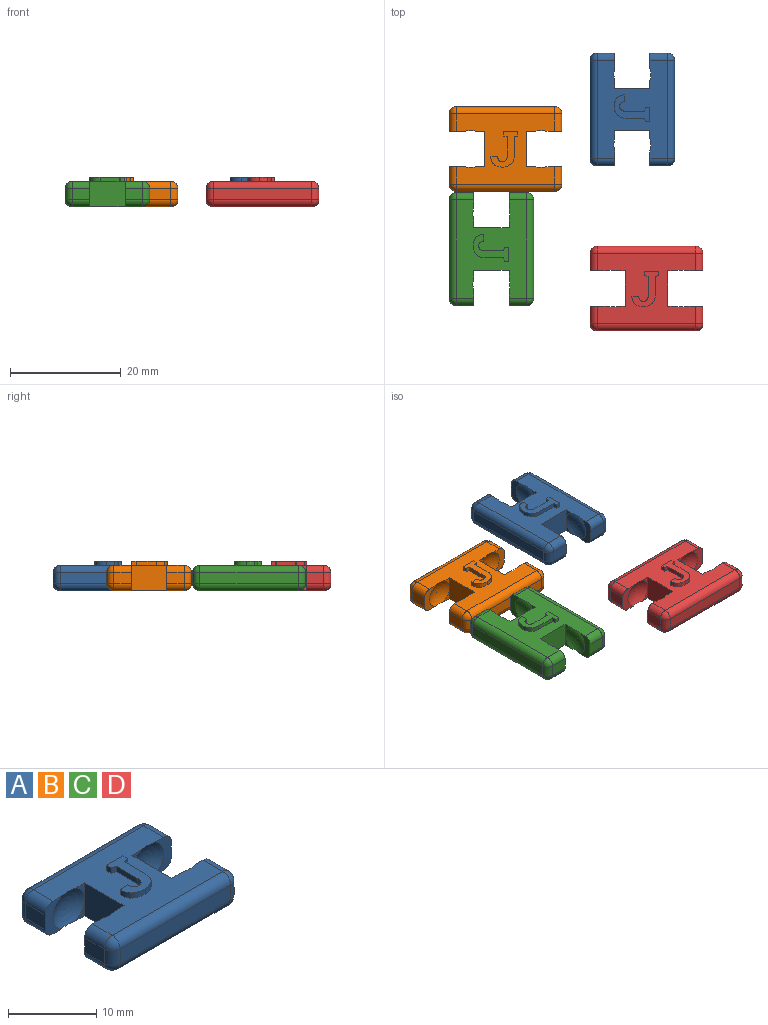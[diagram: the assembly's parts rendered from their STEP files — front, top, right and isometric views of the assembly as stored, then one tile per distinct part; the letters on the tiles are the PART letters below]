
ASSEMBLY  parts=4 mates=3
PART A: 68 faces, bbox 20.3x15.2x5.6 mm
  f0: plane 17.78x12.7mm, normal (0,0,1), area 148.5mm2, adj f2,f4,f6,f7,f9,f11,f14,f15
  f1: plane 17.78x12.7mm, normal (0,0,-1), area 160.4mm2, adj f2,f3,f4,f5,f7,f8,f9,f10
  f2: plane 4.57x2.7mm, normal (0,-1,0), area 7mm2, adj f0,f1,f13,f36,f37,f49
  f3: plane 2.29x1.43mm, normal (0,-1,0), area 0.9mm2, adj f1,f15,f49
  f4: plane 4.57x2.7mm, normal (0,1,0), area 7mm2, adj f0,f1,f16,f26,f27,f48
  f5: plane 2.29x1.43mm, normal (0,1,0), area 0.9mm2, adj f1,f15,f48
  f6: plane 2.29x1.43mm, normal (0,1,0), area 0.9mm2, adj f0,f15,f48
  f7: plane 4.57x2.7mm, normal (0,-1,0), area 7mm2, adj f0,f1,f21,f41,f42,f47
  f8: plane 2.29x1.43mm, normal (0,-1,0), area 0.9mm2, adj f1,f19,f47
  f9: plane 4.57x2.7mm, normal (0,1,0), area 7mm2, adj f0,f1,f18,f31,f32,f46
  f10: plane 2.29x1.43mm, normal (0,1,0), area 0.9mm2, adj f1,f19,f46
  f11: plane 2.29x1.43mm, normal (0,1,0), area 0.9mm2, adj f0,f19,f46
  f12: plane 17.78x2.03mm, normal (0,1,0), area 36.1mm2, adj f23,f25,f40,f45
  f13: plane 3.18x2.03mm, normal (-1,0,0), area 6.5mm2, adj f2,f36,f37,f40
  f14: plane 2.29x1.43mm, normal (0,-1,0), area 0.9mm2, adj f0,f15,f49
  f15: plane 6.35x4.57mm, normal (-1,0,0), area 29mm2, adj f0,f1,f3,f5,f6,f14
  f16: plane 3.18x2.03mm, normal (-1,0,0), area 6.5mm2, adj f4,f26,f27,f30
  f17: plane 17.78x2.03mm, normal (0,-1,0), area 36.1mm2, adj f22,f24,f30,f35
  f18: plane 3.18x2.03mm, normal (1,0,0), area 6.5mm2, adj f9,f31,f32,f35
  f19: plane 6.35x4.57mm, normal (1,0,0), area 29mm2, adj f0,f1,f8,f10,f11,f20
  f20: plane 2.29x1.43mm, normal (0,-1,0), area 0.9mm2, adj f0,f19,f47
  f21: plane 3.18x2.03mm, normal (1,0,0), area 6.5mm2, adj f7,f41,f42,f45
  f22: cylinder r=1.27mm len=17.78mm, axis (1,0,0), area 35.5mm2, adj f1,f17,f29,f34
  f23: cylinder r=1.27mm len=17.78mm, axis (-1,0,0), area 35.5mm2, adj f1,f12,f39,f44
  f24: cylinder r=1.27mm len=17.78mm, axis (-1,0,0), area 35.5mm2, adj f0,f17,f28,f33
  f25: cylinder r=1.27mm len=17.78mm, axis (1,0,0), area 35.5mm2, adj f0,f12,f38,f43
  f26: cylinder r=1.27mm len=3.18mm, axis (0,1,0), area 6.3mm2, adj f0,f4,f16,f28
  f27: cylinder r=1.27mm len=3.18mm, axis (0,-1,0), area 6.3mm2, adj f1,f4,f16,f29
  f28: sphere r=1.27mm, area 2.5mm2, adj f24,f26,f30
  f29: sphere r=1.27mm, area 2.5mm2, adj f22,f27,f30
  f30: cylinder r=1.27mm len=2.03mm, axis (0,0,1), area 4.1mm2, adj f16,f17,f28,f29
  f31: cylinder r=1.27mm len=3.18mm, axis (0,-1,0), area 6.3mm2, adj f0,f9,f18,f33
  f32: cylinder r=1.27mm len=3.18mm, axis (0,1,0), area 6.3mm2, adj f1,f9,f18,f34
  f33: sphere r=1.27mm, area 2.5mm2, adj f24,f31,f35
  f34: sphere r=1.27mm, area 2.5mm2, adj f22,f32,f35
  f35: cylinder r=1.27mm len=2.03mm, axis (0,0,-1), area 4.1mm2, adj f17,f18,f33,f34
  f36: cylinder r=1.27mm len=3.18mm, axis (0,1,0), area 6.3mm2, adj f0,f2,f13,f38
  f37: cylinder r=1.27mm len=3.18mm, axis (0,-1,0), area 6.3mm2, adj f1,f2,f13,f39
  f38: sphere r=1.27mm, area 2.5mm2, adj f25,f36,f40
  f39: sphere r=1.27mm, area 2.5mm2, adj f23,f37,f40
  f40: cylinder r=1.27mm len=2.03mm, axis (0,0,-1), area 4.1mm2, adj f12,f13,f38,f39
  f41: cylinder r=1.27mm len=3.18mm, axis (0,-1,0), area 6.3mm2, adj f0,f7,f21,f43
  f42: cylinder r=1.27mm len=3.18mm, axis (0,1,0), area 6.3mm2, adj f1,f7,f21,f44
  f43: sphere r=1.27mm, area 2.5mm2, adj f25,f41,f45
  f44: sphere r=1.27mm, area 2.5mm2, adj f23,f42,f45
  f45: cylinder r=1.27mm len=2.03mm, axis (0,0,1), area 4.1mm2, adj f12,f21,f43,f44
  f46: sphere r=4.61mm, area 21.2mm2, adj f0,f1,f9,f10,f11
  f47: sphere r=4.61mm, area 21.2mm2, adj f0,f1,f7,f8,f20
  f48: sphere r=4.61mm, area 21.2mm2, adj f0,f1,f4,f5,f6
  f49: sphere r=4.61mm, area 21.2mm2, adj f0,f1,f2,f3,f14
  f50: plane 0.76x0.76mm, normal (1,0,0), area 0.6mm2, adj f0,f51,f66,f67
  f51: plane 2.6x0.76mm, normal (0,1,0), area 2mm2, adj f0,f50,f52,f67
  f52: plane 0.76x0.76mm, normal (-1,0,0), area 0.6mm2, adj f0,f51,f53,f67
  f53: plane 0.76x0.67mm, normal (-0.19,-0.98,0), area 0.5mm2, adj f0,f52,f54,f67
  f54: plane 3.5x0.76mm, normal (-1,0,0), area 2.7mm2, adj f0,f53,f55,f67
  f55: extruded ~0.76x0.74mm, area 0.6mm2, adj f0,f54,f56,f67
  f56: extruded ~0.76x0.59mm, area 0.5mm2, adj f0,f55,f57,f67
  f57: extruded ~0.76x0.64mm, area 0.5mm2, adj f0,f56,f58,f67
  f58: extruded ~0.76x0.72mm, area 0.6mm2, adj f0,f57,f59,f67
  f59: plane 1.22x0.76mm, normal (0,1,0), area 0.9mm2, adj f0,f58,f60,f67
  f60: plane 0.76x0.03mm, normal (-0.94,0.35,0), area 0mm2, adj f0,f59,f61,f67
  f61: extruded ~1.41x0.76mm, area 1.2mm2, adj f0,f60,f62,f67
  f62: extruded ~1.56x0.76mm, area 1.3mm2, adj f0,f61,f63,f67
  f63: extruded ~1.5x0.76mm, area 1.2mm2, adj f0,f62,f64,f67
  f64: extruded ~1.44x0.76mm, area 1.2mm2, adj f0,f63,f65,f67
  f65: plane 3.5x0.76mm, normal (1,0,0), area 2.7mm2, adj f0,f64,f66,f67
  f66: plane 0.76x0.67mm, normal (0.19,-0.98,0), area 0.5mm2, adj f0,f50,f65,f67
  f67: plane 6.36x4.89mm, normal (0,0,1), area 11.9mm2, adj f50,f51,f52,f53,f54,f55,f56,f57
PART B: same geometry as A
PART C: same geometry as A
PART D: same geometry as A
PLACE A rot(axis=(0,0,-1),90deg) t=(-40.12,19.21,4.28)mm
PLACE B t=(-65.52,-5.68,4.28)mm
PLACE C rot(axis=(0,0,-1),90deg) t=(-65.52,-5.93,4.28)mm
PLACE D t=(-40.12,-30.82,4.28)mm
MATE planar C.f0 <-> B.f0  axis (0,0,1) through (-57.87,-16.07,8.85)mm
MATE planar A.f0 <-> B.f0  axis (0,0,1) through (-32.47,9.08,8.85)mm
MATE planar D.f0 <-> A.f0  axis (0,0,1) through (-29.98,-23.18,8.85)mm
